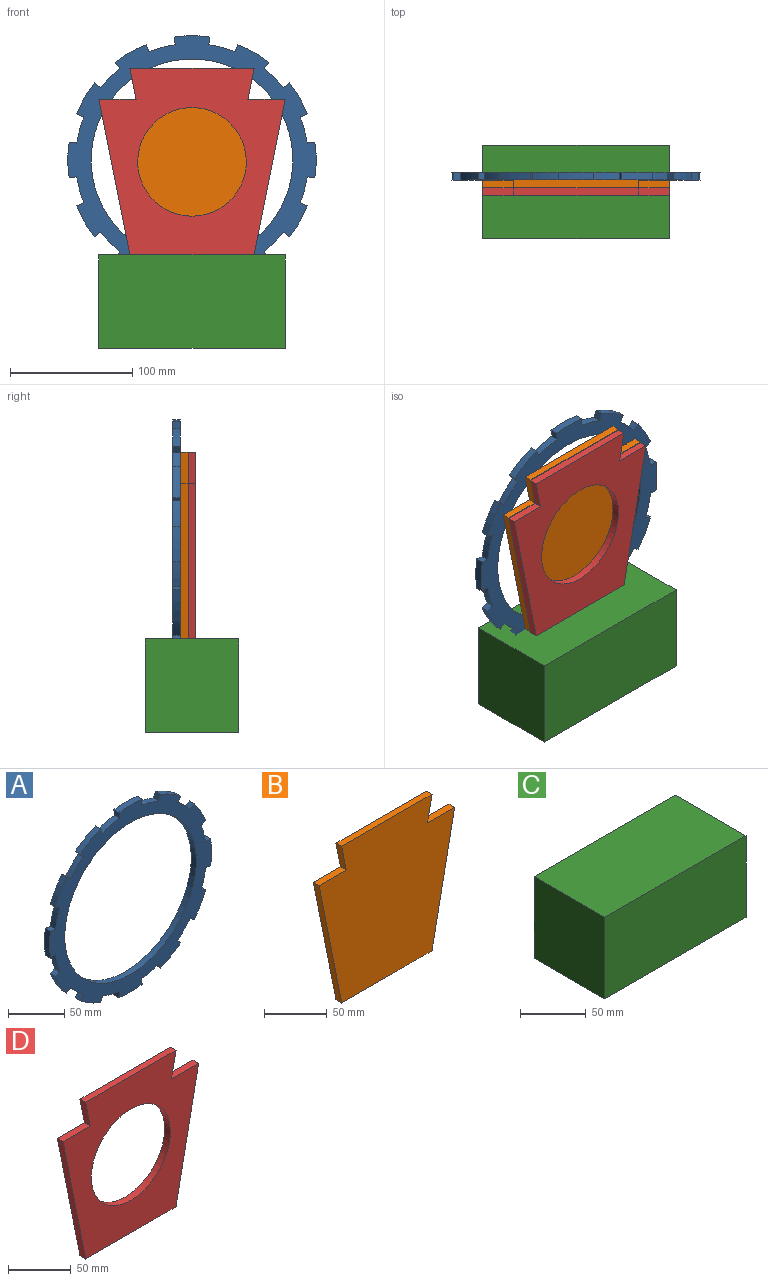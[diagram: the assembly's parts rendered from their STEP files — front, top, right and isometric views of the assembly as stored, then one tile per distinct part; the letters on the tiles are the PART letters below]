
ASSEMBLY  parts=4 mates=3
PART A: 51 faces, bbox 203.2x6.4x203.2 mm
  f0: plane 6.35x4.98mm, normal (0.62,0,0.78), area 40.3mm2, adj f1,f47,f48,f49
  f1: cylinder r=101.6mm len=25.36mm, axis (0,1,0), area 186.6mm2, adj f0,f2,f48,f49
  f2: plane 6.35x5.9mm, normal (-0.37,0,-0.93), area 40.3mm2, adj f1,f3,f48,f49
  f3: cylinder r=95.25mm len=21.52mm, axis (0,1,0), area 141.8mm2, adj f2,f4,f48,f49
  f4: plane 6.35x6.28mm, normal (0.14,0,0.99), area 40.3mm2, adj f3,f5,f48,f49
  f5: cylinder r=101.6mm len=29.28mm, axis (0,1,0), area 186.6mm2, adj f4,f6,f48,f49
  f6: plane 6.35x6.28mm, normal (0.14,0,-0.99), area 40.3mm2, adj f5,f7,f48,f49
  f7: cylinder r=95.25mm len=21.52mm, axis (0,1,0), area 141.8mm2, adj f6,f8,f48,f49
  f8: plane 6.35x5.9mm, normal (-0.37,0,0.93), area 40.3mm2, adj f7,f9,f48,f49
  f9: cylinder r=101.6mm len=25.36mm, axis (0,1,0), area 186.6mm2, adj f8,f10,f48,f49
  f10: plane 6.35x4.98mm, normal (0.62,0,-0.78), area 40.3mm2, adj f9,f11,f48,f49
  f11: cylinder r=95.25mm len=15.75mm, axis (0,1,0), area 141.8mm2, adj f10,f12,f48,f49
  f12: plane 6.35x4.98mm, normal (-0.78,0,0.62), area 40.3mm2, adj f11,f13,f48,f49
  f13: cylinder r=101.6mm len=25.36mm, axis (0,1,0), area 186.6mm2, adj f12,f14,f48,f49
  f14: plane 6.35x5.9mm, normal (0.93,0,-0.37), area 40.3mm2, adj f13,f15,f48,f49
  f15: cylinder r=95.25mm len=21.52mm, axis (0,1,0), area 141.8mm2, adj f14,f16,f48,f49
  f16: plane 6.35x6.28mm, normal (-0.99,0,0.14), area 40.3mm2, adj f15,f17,f48,f49
  f17: cylinder r=101.6mm len=29.28mm, axis (0,1,0), area 186.6mm2, adj f16,f18,f48,f49
  f18: plane 6.35x6.28mm, normal (0.99,0,0.14), area 40.3mm2, adj f17,f19,f48,f49
  f19: cylinder r=95.25mm len=21.52mm, axis (0,1,0), area 141.8mm2, adj f18,f20,f48,f49
  f20: plane 6.35x5.9mm, normal (-0.93,0,-0.37), area 40.3mm2, adj f19,f21,f48,f49
  f21: cylinder r=101.6mm len=25.36mm, axis (0,1,0), area 186.6mm2, adj f20,f22,f48,f49
  f22: plane 6.35x4.98mm, normal (0.78,0,0.62), area 40.3mm2, adj f21,f23,f48,f49
  f23: cylinder r=95.25mm len=15.75mm, axis (0,1,0), area 141.8mm2, adj f22,f24,f48,f49
  f24: plane 6.35x4.98mm, normal (-0.62,0,-0.78), area 40.3mm2, adj f23,f25,f48,f49
  f25: cylinder r=101.6mm len=25.36mm, axis (0,1,0), area 186.6mm2, adj f24,f26,f48,f49
  f26: plane 6.35x5.9mm, normal (0.37,0,0.93), area 40.3mm2, adj f25,f27,f48,f49
  f27: cylinder r=95.25mm len=21.52mm, axis (0,1,0), area 141.8mm2, adj f26,f28,f48,f49
  f28: plane 6.35x6.28mm, normal (-0.14,0,-0.99), area 40.3mm2, adj f27,f29,f48,f49
  f29: cylinder r=101.6mm len=29.28mm, axis (0,1,0), area 186.6mm2, adj f28,f30,f48,f49
  f30: plane 6.35x6.28mm, normal (-0.14,0,0.99), area 40.3mm2, adj f29,f31,f48,f49
  f31: cylinder r=95.25mm len=21.52mm, axis (0,1,0), area 141.8mm2, adj f30,f32,f48,f49
  f32: plane 6.35x5.9mm, normal (0.37,0,-0.93), area 40.3mm2, adj f31,f33,f48,f49
  f33: cylinder r=101.6mm len=25.36mm, axis (0,1,0), area 186.6mm2, adj f32,f34,f48,f49
  f34: plane 6.35x4.98mm, normal (-0.62,0,0.78), area 40.3mm2, adj f33,f35,f48,f49
  f35: cylinder r=95.25mm len=15.75mm, axis (0,1,0), area 141.8mm2, adj f34,f36,f48,f49
  f36: plane 6.35x4.98mm, normal (0.78,0,-0.62), area 40.3mm2, adj f35,f37,f48,f49
  f37: cylinder r=101.6mm len=25.36mm, axis (0,1,0), area 186.6mm2, adj f36,f38,f48,f49
  f38: plane 6.35x5.9mm, normal (-0.93,0,0.37), area 40.3mm2, adj f37,f39,f48,f49
  f39: cylinder r=95.25mm len=21.52mm, axis (0,1,0), area 141.8mm2, adj f38,f40,f48,f49
  f40: plane 6.35x6.28mm, normal (0.99,0,-0.14), area 40.3mm2, adj f39,f41,f48,f49
  f41: cylinder r=101.6mm len=29.28mm, axis (0,1,0), area 186.6mm2, adj f40,f42,f48,f49
  f42: plane 6.35x6.28mm, normal (-0.99,0,-0.14), area 40.3mm2, adj f41,f43,f48,f49
  f43: cylinder r=95.25mm len=21.52mm, axis (0,1,0), area 141.8mm2, adj f42,f44,f48,f49
  f44: plane 6.35x5.9mm, normal (0.93,0,0.37), area 40.3mm2, adj f43,f45,f48,f49
  f45: cylinder r=101.6mm len=25.36mm, axis (0,1,0), area 186.6mm2, adj f44,f46,f48,f49
  f46: plane 6.35x4.98mm, normal (-0.78,0,-0.62), area 40.3mm2, adj f45,f47,f48,f49
  f47: cylinder r=95.25mm len=15.75mm, axis (0,1,0), area 141.8mm2, adj f0,f46,f48,f49
  f48: plane 203.2x203.2mm, normal (0,-1,0), area 9263mm2, adj f0,f1,f2,f3,f4,f5,f6,f7
  f49: plane 203.2x203.2mm, normal (0,1,0), area 9263mm2, adj f0,f1,f2,f3,f4,f5,f6,f7
  f50: cylinder r=82.55mm len=165.1mm, axis (0,-1,0), area 3293.6mm2, adj f48,f49
PART B: 10 faces, bbox 152.4x6.4x152.4 mm
  f0: plane 25.4x6.35mm, normal (0.98,0,-0.2), area 164.5mm2, adj f1,f7,f8,f9
  f1: plane 101.6x6.35mm, normal (0,0,1), area 645.2mm2, adj f0,f2,f8,f9
  f2: plane 25.4x6.35mm, normal (-0.98,0,-0.2), area 164.5mm2, adj f1,f3,f8,f9
  f3: plane 30.48x6.35mm, normal (0,0,1), area 193.5mm2, adj f2,f4,f8,f9
  f4: plane 127x25.4mm, normal (-0.98,0,-0.2), area 822.4mm2, adj f3,f5,f8,f9
  f5: plane 101.6x6.35mm, normal (0,0,-1), area 645.2mm2, adj f4,f6,f8,f9
  f6: plane 127x25.4mm, normal (0.98,0,-0.2), area 822.4mm2, adj f5,f7,f8,f9
  f7: plane 30.48x6.35mm, normal (0,0,1), area 193.5mm2, adj f0,f6,f8,f9
  f8: plane 152.4x152.4mm, normal (0,-1,0), area 18580.6mm2, adj f0,f1,f2,f3,f4,f5,f6,f7
  f9: plane 152.4x152.4mm, normal (0,1,0), area 18580.6mm2, adj f0,f1,f2,f3,f4,f5,f6,f7
PART C: 6 faces, bbox 152.4x76.2x76.2 mm
  f0: plane 152.4x76.2mm, normal (0,0,1), area 11612.9mm2, adj f1,f3,f4,f5
  f1: plane 76.2x76.2mm, normal (-1,0,0), area 5806.4mm2, adj f0,f2,f4,f5
  f2: plane 152.4x76.2mm, normal (0,0,-1), area 11612.9mm2, adj f1,f3,f4,f5
  f3: plane 76.2x76.2mm, normal (1,0,0), area 5806.4mm2, adj f0,f2,f4,f5
  f4: plane 152.4x76.2mm, normal (0,-1,0), area 11612.9mm2, adj f0,f1,f2,f3
  f5: plane 152.4x76.2mm, normal (0,1,0), area 11612.9mm2, adj f0,f1,f2,f3
PART D: 11 faces, bbox 152.4x6.4x152.4 mm
  f0: plane 25.4x6.35mm, normal (0.98,0,-0.2), area 164.5mm2, adj f1,f7,f8,f9
  f1: plane 101.6x6.35mm, normal (0,0,1), area 645.2mm2, adj f0,f2,f8,f9
  f2: plane 25.4x6.35mm, normal (-0.98,0,-0.2), area 164.5mm2, adj f1,f3,f8,f9
  f3: plane 30.48x6.35mm, normal (0,0,1), area 193.5mm2, adj f2,f4,f8,f9
  f4: plane 127x25.4mm, normal (-0.98,0,-0.2), area 822.4mm2, adj f3,f5,f8,f9
  f5: plane 101.6x6.35mm, normal (0,0,-1), area 645.2mm2, adj f4,f6,f8,f9
  f6: plane 127x25.4mm, normal (0.98,0,-0.2), area 822.4mm2, adj f5,f7,f8,f9
  f7: plane 30.48x6.35mm, normal (0,0,1), area 193.5mm2, adj f0,f6,f8,f9
  f8: plane 152.4x152.4mm, normal (0,-1,0), area 12373.4mm2, adj f0,f1,f2,f3,f4,f5,f6,f7
  f9: plane 152.4x152.4mm, normal (0,1,0), area 12373.4mm2, adj f0,f1,f2,f3,f4,f5,f6,f7
  f10: cylinder r=44.45mm len=88.9mm, axis (0,-1,0), area 1773.5mm2, adj f8,f9
PLACE A t=(0,15.87,115.89)mm
PLACE B t=(0,9.52,85.2)mm
PLACE C at identity
PLACE D t=(0,3.17,84.67)mm
MATE fastened D.f5 <-> C.f0  axis (0,0,-1) through (0,0,38.1)mm
MATE fastened A.f41 <-> B.f9  axis (0,-1,0) through (0,9.52,115.89)mm
MATE fastened B.f8 <-> D.f9  axis (0,-1,0) through (0,3.17,115.89)mm
